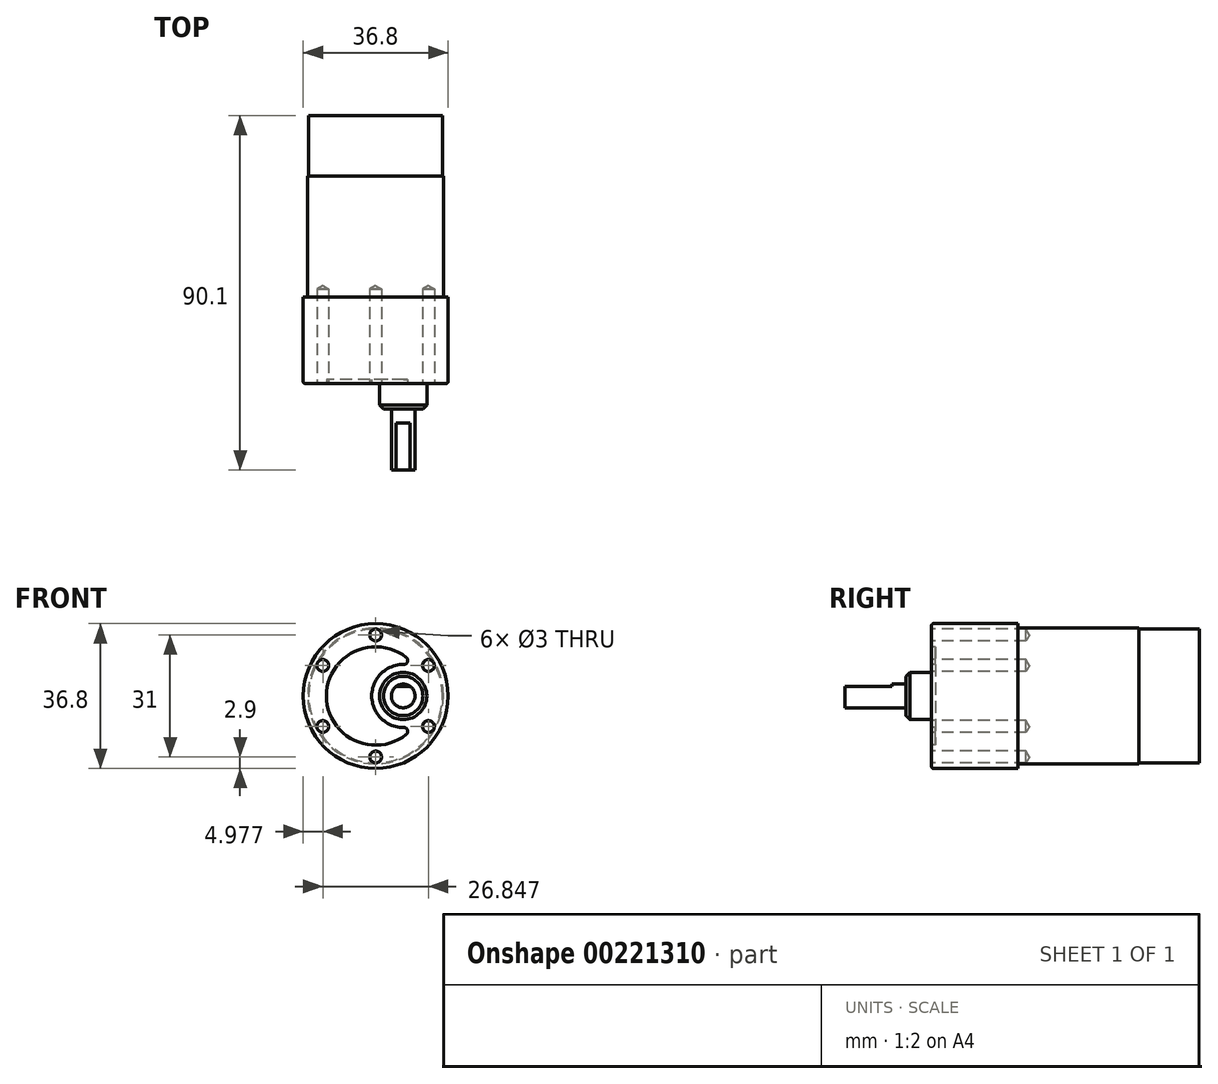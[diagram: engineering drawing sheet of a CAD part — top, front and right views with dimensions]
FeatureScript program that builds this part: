
annotation { "Feature Type Name" : "Feature", "Feature Type Description" : "" }
export const myFeature = defineFeature(function(context is Context, id is Id, definition is map)
    precondition{}
    {
        {
            var Q0;
            Q0=qCreatedBy(makeId("Front.planeOp"),FACE);
            var sketch = newSketch(context, id + "F0", { "sketchPlane" : qUnion([Q0])});
            skCircle(sketch, "E0", {"center": v(0, 0) * mm, "radius": 18.4 * mm});
            skSolve(sketch);
        }
        {
            var Q0;
            Q0=qSketchRegion(id+"F0",true);
            extrude(context, id + "F1", {"entities" : qUnion([Q0]), "depth" : 22 * mm});
        }
        {
            var Q0;
            Q0=makeQuery(id+"F1.opExtrude","CAP_FACE",FACE,{"disambiguationData":[OSD([sQuery(id+"F0.wireOp",EDGE,"E0")])],"isStart":true});
            var sketch = newSketch(context, id + "F2", { "sketchPlane" : qUnion([Q0])});
            skCircle(sketch, "E1", {"center": v(0, 0) * mm, "radius": 17.25 * mm});
            skSolve(sketch);
        }
        {
            var Q0;
            Q0=qSketchRegion(id+"F2",true);
            extrude(context, id + "F3", {"entities" : qUnion([Q0]), "operationType" : NewBodyOperationType.ADD, "depth" : 30.7 * mm});
        }
        {
            var Q0;
            Q0=makeQuery(id+"F1.opExtrude","CAP_FACE",FACE,{"disambiguationData":[OSD([sQuery(id+"F0.wireOp",EDGE,"E0")])],"isStart":false});
            var sketch = newSketch(context, id + "F4", { "sketchPlane" : qUnion([Q0])});
            skCircle(sketch, "E2", {"center": v(7, 0) * mm, "radius": 6 * mm});
            skSolve(sketch);
        }
        {
            var Q0;
            Q0=qSketchRegion(id+"F4",true);
            extrude(context, id + "F5", {"entities" : qUnion([Q0]), "operationType" : NewBodyOperationType.ADD, "depth" : 6.5 * mm});
        }
        {
            var Q0;
            Q0=makeQuery(id+"F5.opExtrude","CAP_FACE",FACE,{"disambiguationData":[OSD([sQuery(id+"F4.wireOp",EDGE,"E2")])],"isStart":false});
            var sketch = newSketch(context, id + "F6", { "sketchPlane" : qUnion([Q0])});
            skCircle(sketch, "E3", {"center": v(7, 0) * mm, "radius": 3 * mm});
            skSolve(sketch);
        }
        {
            var Q0;
            Q0=qSketchRegion(id+"F6",true);
            extrude(context, id + "F7", {"entities" : qUnion([Q0]), "operationType" : NewBodyOperationType.ADD, "depth" : 15.5 * mm});
        }
        {
            var Q0;
            Q0=makeQuery(id+"F5.opExtrude","CAP_EDGE",EDGE,{"disambiguationData":[OSD([sQuery(id+"F4.wireOp",EDGE,"E2")])],"isStart":false});
            chamfer(context, id + "F8", {"entities" : qUnion([Q0]), "width" : 1 * mm, "tangentPropagation" : true});
        }
        {
            var Q0;
            Q0=makeQuery(id+"F7.opExtrude","CAP_FACE",FACE,{"disambiguationData":[OSD([sQuery(id+"F6.wireOp",EDGE,"E3")])],"isStart":false});
            var sketch = newSketch(context, id + "F9", { "sketchPlane" : qUnion([Q0])});
            skLineSegment(sketch, "E4", {"start": v(5.2, 2.4) * mm, "end": v(8.8, 2.4) * mm});
            skArc(sketch, "E5", {"start": v(8.8, 2.4) * mm, "mid": v(7, 3) * mm, "end": v(5.2, 2.4) * mm});
            skSolve(sketch);
        }
        {
            var Q0;
            Q0=makeQuery(id+"F9.imprint","IMPRINT",FACE,{"disambiguationData":[TD([[makeQuery(id+"F9.imprint","IMPRINT",EDGE,{"derivedFrom":sQuery(id+"F9.wireOp",EDGE,"E4")}),1.0]])]});
            extrude(context, id + "F10", {"entities" : qUnion([Q0]), "operationType" : NewBodyOperationType.REMOVE, "oppositeDirection" : true, "depth" : 12 * mm});
        }
        {
            var Q0;
            Q0=makeQuery(id+"F1.opExtrude","CAP_FACE",FACE,{"disambiguationData":[OSD([sQuery(id+"F0.wireOp",EDGE,"E0")])],"isStart":false});
            var sketch = newSketch(context, id + "F11", { "sketchPlane" : qUnion([Q0])});
            skCircle(sketch, "E6", {"center": v(0, 15.5) * mm, "radius": 1.5 * mm});
            skCircle(sketch, "E7.1.0", {"center": v(-13.42, 7.75) * mm, "radius": 1.5 * mm});
            skCircle(sketch, "E7.2.0", {"center": v(-13.42, -7.75) * mm, "radius": 1.5 * mm});
            skCircle(sketch, "E7.3.0", {"center": v(0, -15.5) * mm, "radius": 1.5 * mm});
            skCircle(sketch, "E7.4.0", {"center": v(13.42, -7.75) * mm, "radius": 1.5 * mm});
            skCircle(sketch, "E7.5.0", {"center": v(13.42, 7.75) * mm, "radius": 1.5 * mm});
            skPoint(sketch, "E7.center", {"position": v(0, 0) * mm});
            skSolve(sketch);
        }
        {
            var Q0;
            Q0=sQuery(id+"F11.wireOp",VERTEX,"E6.center");
            var Q1;
            Q1=sQuery(id+"F11.wireOp",VERTEX,"E7.1.0.center");
            var Q2;
            Q2=sQuery(id+"F11.wireOp",VERTEX,"E7.2.0.center");
            var Q3;
            Q3=sQuery(id+"F11.wireOp",VERTEX,"E7.3.0.center");
            var Q4;
            Q4=sQuery(id+"F11.wireOp",VERTEX,"E7.4.0.center");
            var Q5;
            Q5=sQuery(id+"F11.wireOp",VERTEX,"E7.5.0.center");
            var Q6;
            Q6=makeQuery(id+"F1.opExtrude","SWEPT_BODY",BODY,{"disambiguationData":[OSD([sQuery(id+"F0.wireOp",EDGE,"E0")])]});
            hole(context, id + "F12", {"style" : HoleStyle.SIMPLE, "holeDiameter" : 3 * mm, "endStyle" : HoleEndStyle.BLIND, "holeDepth" : 24 * mm, "locations" : qUnion([Q0, Q1, Q2, Q3, Q4, Q5]), "scope" : qUnion([Q6])});
        }
        {
            var Q0;
            Q0=makeQuery(id+"F1.opExtrude","CAP_FACE",FACE,{"disambiguationData":[OSD([sQuery(id+"F0.wireOp",EDGE,"E0")])],"isStart":false});
            var sketch = newSketch(context, id + "F13", { "sketchPlane" : qUnion([Q0])});
            skArc(sketch, "E8", {"start": v(7.78, 9.78) * mm, "mid": v(-12.5, 0) * mm, "end": v(7.78, -9.78) * mm});
            skArc(sketch, "E9", {"start": v(7.14, 8) * mm, "mid": v(-1, 0) * mm, "end": v(7.14, -8) * mm});
            skPoint(sketch, "E10.visualSharp", {"position": v(10.09, 7.38) * mm});
            skArc(sketch, "E10.filletArc", {"start": v(7.14, 8) * mm, "mid": v(8.1, 8.66) * mm, "end": v(7.78, 9.78) * mm});
            skPoint(sketch, "E11.visualSharp", {"position": v(10.09, -7.38) * mm});
            skArc(sketch, "E11.filletArc", {"start": v(7.78, -9.78) * mm, "mid": v(8.1, -8.66) * mm, "end": v(7.14, -8) * mm});
            skSolve(sketch);
        }
        {
            var Q0;
            Q0=makeQuery(id+"F13.imprint","IMPRINT",FACE,{"disambiguationData":[TD([[makeQuery(id+"F13.imprint","IMPRINT",EDGE,{"derivedFrom":sQuery(id+"F13.wireOp",EDGE,"E8")}),1.0]])]});
            extrude(context, id + "F14", {"entities" : qUnion([Q0]), "operationType" : NewBodyOperationType.REMOVE, "oppositeDirection" : true, "depth" : 1 * mm});
        }
        {
            var Q0;
            Q0=makeQuery(id+"F3.opExtrude","CAP_FACE",FACE,{"disambiguationData":[OSD([sQuery(id+"F2.wireOp",EDGE,"E1")])],"isStart":false});
            var sketch = newSketch(context, id + "F15", { "sketchPlane" : qUnion([Q0])});
            skCircle(sketch, "E12", {"center": v(0, 0) * mm, "radius": 6.5 * mm});
            skSolve(sketch);
        }
        {
            var Q0;
            Q0=makeQuery(id+"F15.imprint","IMPRINT",FACE,{"disambiguationData":[TD([[makeQuery(id+"F15.imprint","IMPRINT",EDGE,{"derivedFrom":sQuery(id+"F15.wireOp",EDGE,"E12")}),1.0]])]});
            extrude(context, id + "F16", {"entities" : qUnion([Q0]), "operationType" : NewBodyOperationType.ADD, "depth" : 1.5 * mm});
        }
        {
            var Q0;
            Q0=makeQuery(id+"F16.opExtrude","CAP_EDGE",EDGE,{"disambiguationData":[OSD([sQuery(id+"F15.wireOp",EDGE,"E12")])],"isStart":false});
            chamfer(context, id + "F17", {"entities" : qUnion([Q0]), "width" : 1 * mm, "tangentPropagation" : true});
        }
        {
            var Q0;
            Q0=makeQuery(id+"F3.opExtrude","CAP_FACE",FACE,{"disambiguationData":[OSD([sQuery(id+"F2.wireOp",EDGE,"E1")])],"isStart":false});
            var sketch = newSketch(context, id + "F18", { "sketchPlane" : qUnion([Q0])});
            skLineSegment(sketch, "E13.bottom", {"start": v(-1.59, 12.05) * mm, "end": v(1.59, 12.05) * mm});
            skLineSegment(sketch, "E13.top", {"start": v(-1.59, 11.26) * mm, "end": v(1.59, 11.26) * mm});
            skLineSegment(sketch, "E13.left", {"start": v(-1.59, 12.05) * mm, "end": v(-1.59, 11.26) * mm});
            skLineSegment(sketch, "E13.right", {"start": v(1.59, 12.05) * mm, "end": v(1.59, 11.26) * mm});
            skLineSegment(sketch, "E14", {"start": v(0, 0) * mm, "end": v(0, 12.05) * mm, "construction": true});
            skLineSegment(sketch, "E15", {"start": v(0, 0) * mm, "end": v(8.8, 0) * mm, "construction": true});
            skLineSegment(sketch, "E16.MirrorCS", {"start": v(-1.59, -12.05) * mm, "end": v(1.59, -12.05) * mm});
            skLineSegment(sketch, "E17.MirrorCS", {"start": v(-1.59, -12.05) * mm, "end": v(-1.59, -11.26) * mm});
            skLineSegment(sketch, "E18.MirrorCS", {"start": v(-1.59, -11.26) * mm, "end": v(1.59, -11.26) * mm});
            skLineSegment(sketch, "E19.MirrorCS", {"start": v(1.59, -12.05) * mm, "end": v(1.59, -11.26) * mm});
            skSolve(sketch);
        }
        {
            var Q0;
            Q0=makeQuery(id+"F18.imprint","IMPRINT",FACE,{"disambiguationData":[TD([[makeQuery(id+"F18.imprint","IMPRINT",EDGE,{"derivedFrom":sQuery(id+"F18.wireOp",EDGE,"E13.bottom")}),-1.0]])]});
            var Q1;
            Q1=makeQuery(id+"F18.imprint","IMPRINT",FACE,{"disambiguationData":[TD([[makeQuery(id+"F18.imprint","IMPRINT",EDGE,{"derivedFrom":sQuery(id+"F18.wireOp",EDGE,"E16.MirrorCS")}),1.0]])]});
            extrude(context, id + "F19", {"entities" : qUnion([Q0, Q1]), "operationType" : NewBodyOperationType.ADD, "depth" : 5.6 * mm});
        }
        {
            var Q0;
            Q0=makeQuery(id+"F19.opExtrude","CAP_EDGE",EDGE,{"disambiguationData":[OSD([sQuery(id+"F18.wireOp",EDGE,"E13.right")])],"isStart":false});
            var Q1;
            Q1=makeQuery(id+"F19.opExtrude","CAP_EDGE",EDGE,{"disambiguationData":[OSD([sQuery(id+"F18.wireOp",EDGE,"E13.left")])],"isStart":false});
            var Q2;
            Q2=makeQuery(id+"F19.opExtrude","CAP_EDGE",EDGE,{"disambiguationData":[OSD([sQuery(id+"F18.wireOp",EDGE,"E17.MirrorCS")])],"isStart":false});
            var Q3;
            Q3=makeQuery(id+"F19.opExtrude","CAP_EDGE",EDGE,{"disambiguationData":[OSD([sQuery(id+"F18.wireOp",EDGE,"E19.MirrorCS")])],"isStart":false});
            chamfer(context, id + "F20", {"entities" : qUnion([Q0, Q1, Q2, Q3]), "width" : 1 * mm, "tangentPropagation" : true});
        }
        {
            var Q0;
            Q0=makeQuery(id+"F19.opExtrude","SWEPT_FACE",FACE,{"disambiguationData":[OSD([sQuery(id+"F18.wireOp",EDGE,"E13.bottom")])]});
            var sketch = newSketch(context, id + "F21", { "sketchPlane" : qUnion([Q0])});
            skArc(sketch, "E20", {"start": v(0.5, 35) * mm, "mid": v(0, 35.5) * mm, "end": v(-0.5, 35) * mm});
            skArc(sketch, "E21", {"start": v(-0.5, 33.74) * mm, "mid": v(0, 33.24) * mm, "end": v(0.5, 33.74) * mm});
            skLineSegment(sketch, "E22", {"start": v(-0.5, 35) * mm, "end": v(-0.5, 33.74) * mm});
            skLineSegment(sketch, "E23", {"start": v(0.5, 35) * mm, "end": v(0.5, 33.74) * mm});
            skSolve(sketch);
        }
        {
            var Q0;
            Q0=qSketchRegion(id+"F21",true);
            extrude(context, id + "F22", {"entities" : qUnion([Q0]), "operationType" : NewBodyOperationType.REMOVE, "oppositeDirection" : true, "depth" : 25.4 * mm});
        }
        {
            var Q0;
            Q0=makeQuery(id+"F1.opExtrude","CAP_EDGE",EDGE,{"disambiguationData":[OSD([sQuery(id+"F0.wireOp",EDGE,"E0")])],"isStart":false});
            fillet(context, id + "F23", {"entities" : qUnion([Q0]), "radius" : .5 * mm, "tangentPropagation" : true, "allowEdgeOverflow" : false});
        }
        {
            var Q0;
            Q0=makeQuery(id+"F3.opExtrude","CAP_FACE",FACE,{"disambiguationData":[OSD([sQuery(id+"F2.wireOp",EDGE,"E1")])],"isStart":false});
            var sketch = newSketch(context, id + "F24", { "sketchPlane" : qUnion([Q0])});
            skCircle(sketch, "E24", {"center": v(0, 0) * mm, "radius": 17 * mm});
            skSolve(sketch);
        }
        {
            var Q0;
            Q0 = qSketchRegion(id + "F24", true);
            extrude(context, id + "F25", {"entities" : qUnion([Q0]), "operationType" : NewBodyOperationType.ADD, "depth" : 15.4 * mm});
        }
    });
